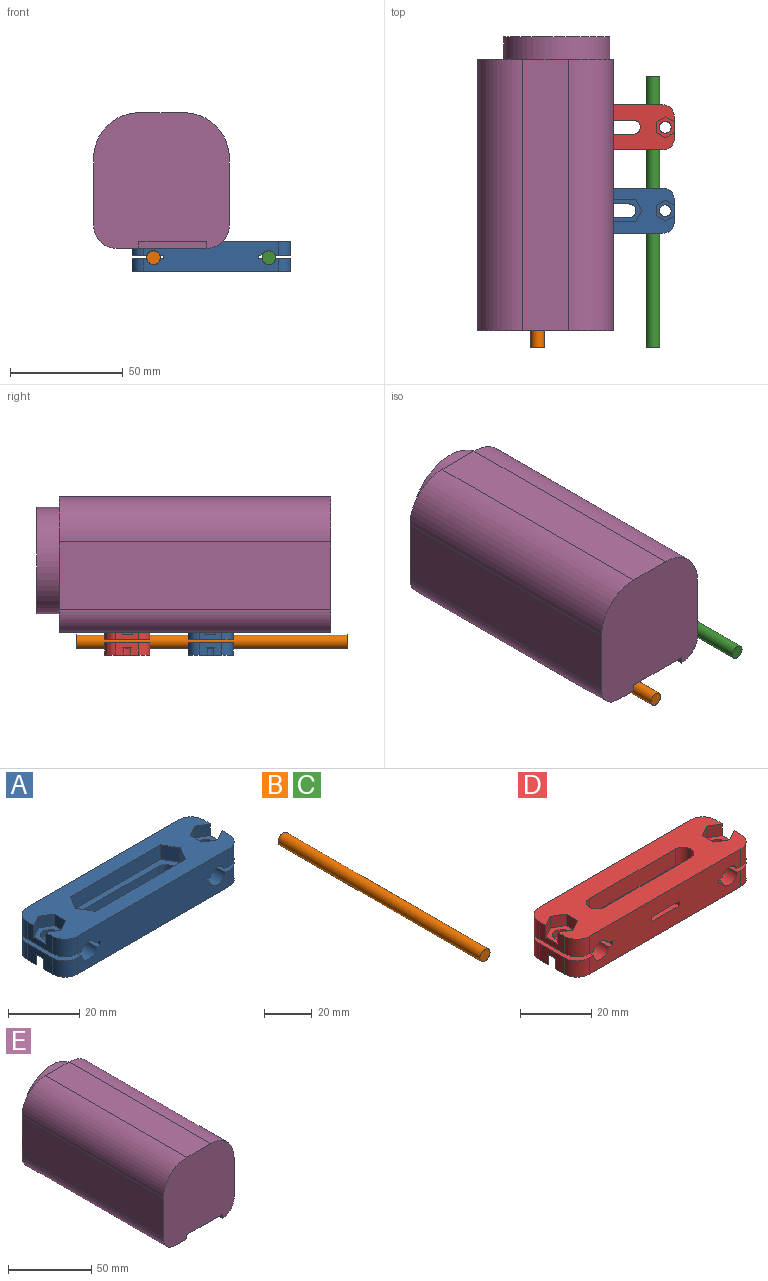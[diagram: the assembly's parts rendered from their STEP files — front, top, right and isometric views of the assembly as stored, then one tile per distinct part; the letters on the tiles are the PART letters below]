
ASSEMBLY  parts=5 mates=5
PART A: 61 faces, bbox 70x20x13 mm
  f0: plane 70x20mm, normal (0,0,1), area 881.1mm2, adj f12,f13,f14,f15,f19,f20,f21,f22
  f1: cylinder r=3mm len=8mm, axis (0,0,1), area 75.4mm2, adj f2,f4,f6,f60
  f2: plane 30x8mm, normal (0,-1,0), area 240mm2, adj f1,f3,f6,f60
  f3: cylinder r=3mm len=8mm, axis (0,0,1), area 75.4mm2, adj f2,f4,f6,f60
  f4: plane 30x8mm, normal (0,1,0), area 240mm2, adj f1,f3,f6,f60
  f5: cylinder r=2.6mm len=5.2mm, axis (0,0,1), area 33.3mm2, adj f34,f48,f51
  f6: plane 70x20mm, normal (0,0,-1), area 1057.7mm2, adj f1,f2,f3,f4,f14,f15,f17,f18
  f7: cylinder r=2.6mm len=5.2mm, axis (0,0,1), area 33.3mm2, adj f37,f46,f53
  f8: plane 20x1.57mm, normal (0,0,-1), area 31.3mm2, adj f14,f15,f32,f49
  f9: plane 20x1.43mm, normal (0,0,1), area 28.5mm2, adj f14,f15,f32,f48
  f10: plane 20x1.57mm, normal (0,0,-1), area 31.3mm2, adj f14,f15,f35,f47
  f11: plane 20x1.43mm, normal (0,0,1), area 28.5mm2, adj f14,f15,f35,f46
  f12: plane 10x6mm, normal (-1,0,0), area 41.5mm2, adj f0,f25,f26,f30,f36,f44,f45
  f13: plane 10x6mm, normal (1,0,0), area 41.5mm2, adj f0,f19,f23,f24,f33,f42,f43
  f14: plane 60x13mm, normal (0,-1,0), area 711.5mm2, adj f0,f6,f8,f9,f10,f11,f32,f33
  f15: plane 60x13mm, normal (0,1,0), area 711.5mm2, adj f0,f6,f8,f9,f10,f11,f32,f33
  f16: cylinder r=2.6mm len=5.2mm, axis (0,0,1), area 32.6mm2, adj f30,f36,f47
  f17: plane 10x5.6mm, normal (-1,0,0), area 45.9mm2, adj f6,f37,f38,f41,f52,f53
  f18: plane 10x5.6mm, normal (1,0,0), area 45.9mm2, adj f6,f34,f39,f40,f50,f51
  f19: plane 4x4mm, normal (-0.5,-0.87,0), area 18.5mm2, adj f0,f13,f20,f24
  f20: plane 4x4mm, normal (0.5,-0.87,0), area 18.5mm2, adj f0,f19,f21,f24
  f21: plane 4.62x4mm, normal (1,0,0), area 18.5mm2, adj f0,f20,f22,f24
  f22: plane 4x4mm, normal (0.5,0.87,0), area 18.5mm2, adj f0,f21,f23,f24
  f23: plane 4x4mm, normal (-0.5,0.87,0), area 18.5mm2, adj f0,f13,f22,f24
  f24: plane 9.24x8mm, normal (0,0,1), area 34.2mm2, adj f13,f19,f20,f21,f22,f23,f31
  f25: plane 4x4mm, normal (0.5,-0.87,0), area 18.5mm2, adj f0,f12,f29,f30
  f26: plane 4x4mm, normal (0.5,0.87,0), area 18.5mm2, adj f0,f12,f27,f30
  f27: plane 4x4mm, normal (-0.5,0.87,0), area 18.5mm2, adj f0,f26,f28,f30
  f28: plane 4.62x4mm, normal (-1,0,0), area 18.5mm2, adj f0,f27,f29,f30
  f29: plane 4x4mm, normal (-0.5,-0.87,0), area 18.5mm2, adj f0,f25,f28,f30
  f30: plane 9.24x8mm, normal (0,0,1), area 34.2mm2, adj f12,f16,f25,f26,f27,f28,f29
  f31: cylinder r=2.6mm len=5.2mm, axis (0,0,1), area 32.6mm2, adj f24,f33,f49
  f32: plane 20x1.4mm, normal (1,0,0), area 28mm2, adj f8,f9,f14,f15
  f33: plane 20x6.57mm, normal (0,0,-1), area 99.4mm2, adj f13,f14,f15,f31,f42,f43,f49
  f34: plane 20x6.43mm, normal (0,0,1), area 96.8mm2, adj f5,f14,f15,f18,f39,f40,f48
  f35: plane 20x1.4mm, normal (-1,0,0), area 28mm2, adj f10,f11,f14,f15
  f36: plane 20x6.57mm, normal (0,0,-1), area 99.4mm2, adj f12,f14,f15,f16,f44,f45,f47
  f37: plane 20x6.43mm, normal (0,0,1), area 96.8mm2, adj f7,f14,f15,f17,f38,f41,f46
  f38: cylinder r=5mm len=5.6mm, axis (0,0,-1), area 44mm2, adj f6,f14,f17,f37
  f39: cylinder r=5mm len=5.6mm, axis (0,0,1), area 44mm2, adj f6,f14,f18,f34
  f40: cylinder r=5mm len=5.6mm, axis (0,0,-1), area 44mm2, adj f6,f15,f18,f34
  f41: cylinder r=5mm len=5.6mm, axis (0,0,1), area 44mm2, adj f6,f15,f17,f37
  f42: cylinder r=5mm len=6mm, axis (0,0,1), area 47.1mm2, adj f0,f13,f14,f33
  f43: cylinder r=5mm len=6mm, axis (0,0,-1), area 47.1mm2, adj f0,f13,f15,f33
  f44: cylinder r=5mm len=6mm, axis (0,0,1), area 47.1mm2, adj f0,f12,f15,f36
  f45: cylinder r=5mm len=6mm, axis (0,0,-1), area 47.1mm2, adj f0,f12,f14,f36
  f46: cylinder r=3.1mm len=20mm, axis (0,-1,0), area 175.8mm2, adj f7,f11,f14,f15,f37,f52,f53
  f47: cylinder r=3.1mm len=20mm, axis (0,-1,0), area 154mm2, adj f10,f14,f15,f16,f36
  f48: cylinder r=3.1mm len=20mm, axis (0,-1,0), area 175.8mm2, adj f5,f9,f14,f15,f34,f50,f51
  f49: cylinder r=3.1mm len=20mm, axis (0,-1,0), area 154mm2, adj f8,f14,f15,f31,f33
  f50: cylinder r=4.25mm len=8.5mm, axis (0,0,-1), area 82.2mm2, adj f6,f18,f48,f51
  f51: plane 8.5x7.67mm, normal (0,0,-1), area 33.3mm2, adj f5,f18,f48,f50
  f52: cylinder r=4.25mm len=8.5mm, axis (0,0,-1), area 82.2mm2, adj f6,f17,f46,f53
  f53: plane 8.5x7.67mm, normal (0,0,-1), area 33.3mm2, adj f7,f17,f46,f52
  f54: plane 5x5mm, normal (-0.87,-0.5,0), area 28.9mm2, adj f0,f55,f59,f60
  f55: plane 35.77x5mm, normal (0,-1,0), area 178.9mm2, adj f0,f54,f56,f60
  f56: plane 5x5mm, normal (0.87,-0.5,0), area 28.9mm2, adj f0,f55,f57,f60
  f57: plane 5x5mm, normal (0.87,0.5,0), area 28.9mm2, adj f0,f56,f58,f60
  f58: plane 35.77x5mm, normal (0,1,0), area 178.9mm2, adj f0,f57,f59,f60
  f59: plane 5x5mm, normal (-0.87,0.5,0), area 28.9mm2, adj f0,f54,f58,f60
  f60: plane 41.55x10mm, normal (0,0,1), area 178.3mm2, adj f1,f2,f3,f4,f54,f55,f56,f57
PART B: 3 faces, bbox 6x120x6 mm
  f0: cylinder r=3mm len=120mm, axis (0,1,0), area 2261.9mm2, adj f1,f2
  f1: plane 6x6mm, normal (0,-1,0), area 28.3mm2, adj f0
  f2: plane 6x6mm, normal (0,1,0), area 28.3mm2, adj f0
PART C: same geometry as B
PART D: 67 faces, bbox 70x20x13 mm
  f0: cylinder r=2.6mm len=5.2mm, axis (0,0,1), area 33.3mm2, adj f13,f59,f66
  f1: plane 70x20mm, normal (0,0,-1), area 1033.7mm2, adj f6,f7,f9,f10,f17,f18,f19,f20
  f2: cylinder r=2.6mm len=5.2mm, axis (0,0,1), area 33.3mm2, adj f21,f61,f64
  f3: plane 10x6mm, normal (-1,0,0), area 41.5mm2, adj f11,f12,f22,f31,f32,f36,f62
  f4: plane 10x6mm, normal (1,0,0), area 41.5mm2, adj f22,f25,f29,f30,f42,f43,f60
  f5: cylinder r=3.1mm len=20mm, axis (0,-1,0), area 154mm2, adj f6,f7,f8,f57,f62
  f6: plane 60x13mm, normal (0,-1,0), area 693.9mm2, adj f1,f5,f9,f12,f13,f15,f21,f22
  f7: plane 60x13mm, normal (0,1,0), area 711.5mm2, adj f1,f5,f10,f11,f13,f21,f22,f43
  f8: cylinder r=2.6mm len=5.2mm, axis (0,0,1), area 32.6mm2, adj f5,f36,f62
  f9: cylinder r=5mm len=5.6mm, axis (0,0,1), area 44mm2, adj f1,f6,f24,f59
  f10: cylinder r=5mm len=5.6mm, axis (0,0,-1), area 44mm2, adj f1,f7,f24,f59
  f11: cylinder r=5mm len=6mm, axis (0,0,1), area 47.1mm2, adj f3,f7,f22,f62
  f12: cylinder r=5mm len=6mm, axis (0,0,-1), area 47.1mm2, adj f3,f6,f22,f62
  f13: cylinder r=3.1mm len=20mm, axis (0,-1,0), area 175.8mm2, adj f0,f6,f7,f55,f59,f65,f66
  f14: plane 11x0.3mm, normal (1,0,0), area 3.3mm2, adj f48,f49,f50,f57
  f15: plane 42x15.5mm, normal (0,0,1), area 279.2mm2, adj f6,f16,f17,f18,f19,f20,f48,f49
  f16: plane 17x1.6mm, normal (0,1,0), area 25.2mm2, adj f15,f47,f50,f51,f53,f54
  f17: cylinder r=3mm len=6mm, axis (0,0,1), area 53.7mm2, adj f1,f15,f18,f20
  f18: plane 34x5.7mm, normal (0,-1,0), area 193.8mm2, adj f1,f15,f17,f19
  f19: cylinder r=3mm len=6mm, axis (0,0,1), area 53.7mm2, adj f1,f15,f18,f20
  f20: plane 34x5.7mm, normal (0,1,0), area 193.8mm2, adj f1,f15,f17,f19
  f21: cylinder r=3.1mm len=20mm, axis (0,-1,0), area 175.8mm2, adj f2,f6,f7,f58,f61,f63,f64
  f22: plane 70x20mm, normal (0,0,1), area 1035.4mm2, adj f3,f4,f6,f7,f11,f12,f25,f26
  f23: plane 10x5.6mm, normal (-1,0,0), area 45.9mm2, adj f1,f44,f45,f61,f63,f64
  f24: plane 10x5.6mm, normal (1,0,0), area 45.9mm2, adj f1,f9,f10,f59,f65,f66
  f25: plane 4x4mm, normal (-0.5,-0.87,0), area 18.5mm2, adj f4,f22,f26,f30
  f26: plane 4x4mm, normal (0.5,-0.87,0), area 18.5mm2, adj f22,f25,f27,f30
  f27: plane 4.62x4mm, normal (1,0,0), area 18.5mm2, adj f22,f26,f28,f30
  f28: plane 4x4mm, normal (0.5,0.87,0), area 18.5mm2, adj f22,f27,f29,f30
  f29: plane 4x4mm, normal (-0.5,0.87,0), area 18.5mm2, adj f4,f22,f28,f30
  f30: plane 9.24x8mm, normal (0,0,1), area 34.2mm2, adj f4,f25,f26,f27,f28,f29,f37
  f31: plane 4x4mm, normal (0.5,-0.87,0), area 18.5mm2, adj f3,f22,f35,f36
  f32: plane 4x4mm, normal (0.5,0.87,0), area 18.5mm2, adj f3,f22,f33,f36
  f33: plane 4x4mm, normal (-0.5,0.87,0), area 18.5mm2, adj f22,f32,f34,f36
  f34: plane 4.62x4mm, normal (-1,0,0), area 18.5mm2, adj f22,f33,f35,f36
  f35: plane 4x4mm, normal (-0.5,-0.87,0), area 18.5mm2, adj f22,f31,f34,f36
  f36: plane 9.24x8mm, normal (0,0,1), area 34.2mm2, adj f3,f8,f31,f32,f33,f34,f35
  f37: cylinder r=2.6mm len=5.2mm, axis (0,0,1), area 32.6mm2, adj f30,f46,f60
  f38: cylinder r=3mm len=6mm, axis (0,0,1), area 53.7mm2, adj f22,f39,f41,f50
  f39: plane 34x5.7mm, normal (0,-1,0), area 193.8mm2, adj f22,f38,f40,f50
  f40: cylinder r=3mm len=6mm, axis (0,0,1), area 53.7mm2, adj f22,f39,f41,f50
  f41: plane 34x5.7mm, normal (0,1,0), area 193.8mm2, adj f22,f38,f40,f50
  f42: cylinder r=5mm len=6mm, axis (0,0,1), area 47.1mm2, adj f4,f6,f22,f60
  f43: cylinder r=5mm len=6mm, axis (0,0,-1), area 47.1mm2, adj f4,f7,f22,f60
  f44: cylinder r=5mm len=5.6mm, axis (0,0,1), area 44mm2, adj f1,f7,f23,f61
  f45: cylinder r=5mm len=5.6mm, axis (0,0,-1), area 44mm2, adj f1,f6,f23,f61
  f46: cylinder r=3.1mm len=20mm, axis (0,-1,0), area 154mm2, adj f6,f7,f37,f54,f60
  f47: plane 11x0.3mm, normal (-1,0,0), area 3.3mm2, adj f16,f49,f50,f54
  f48: plane 17x1.6mm, normal (0,1,0), area 25.3mm2, adj f14,f15,f50,f52,f56,f57
  f49: plane 45x1.6mm, normal (0,-1,0), area 68.1mm2, adj f14,f15,f47,f50,f53,f54,f56,f57
  f50: plane 45x15.5mm, normal (0,0,-1), area 312.2mm2, adj f6,f14,f16,f38,f39,f40,f41,f47
  f51: plane 4.5x1.6mm, normal (-1,0,0), area 7.2mm2, adj f6,f15,f16,f50
  f52: plane 4.5x1.6mm, normal (1,0,0), area 7.2mm2, adj f6,f15,f48,f50
  f53: plane 20x1.4mm, normal (1,0,0), area 13.7mm2, adj f6,f7,f15,f16,f49,f54,f55
  f54: plane 20x1.57mm, normal (0,0,-1), area 14.8mm2, adj f6,f7,f16,f46,f47,f49,f53
  f55: plane 20x1.43mm, normal (0,0,1), area 28.5mm2, adj f6,f7,f13,f53
  f56: plane 20x1.4mm, normal (-1,0,0), area 13.7mm2, adj f6,f7,f15,f48,f49,f57,f58
  f57: plane 20x1.57mm, normal (0,0,-1), area 14.8mm2, adj f5,f6,f7,f14,f48,f49,f56
  f58: plane 20x1.43mm, normal (0,0,1), area 28.5mm2, adj f6,f7,f21,f56
  f59: plane 20x6.43mm, normal (0,0,1), area 96.8mm2, adj f0,f6,f7,f9,f10,f13,f24
  f60: plane 20x6.57mm, normal (0,0,-1), area 99.4mm2, adj f4,f6,f7,f37,f42,f43,f46
  f61: plane 20x6.43mm, normal (0,0,1), area 96.8mm2, adj f2,f6,f7,f21,f23,f44,f45
  f62: plane 20x6.57mm, normal (0,0,-1), area 99.4mm2, adj f3,f5,f6,f7,f8,f11,f12
  f63: cylinder r=4.25mm len=8.5mm, axis (0,0,-1), area 82.2mm2, adj f1,f21,f23,f64
  f64: plane 8.5x7.67mm, normal (0,0,-1), area 33.3mm2, adj f2,f21,f23,f63
  f65: cylinder r=4.25mm len=8.5mm, axis (0,0,-1), area 82.2mm2, adj f1,f13,f24,f66
  f66: plane 8.5x7.67mm, normal (0,0,-1), area 33.3mm2, adj f0,f13,f24,f65
PART E: 18 faces, bbox 60x130x60 mm
  f0: plane 60x60mm, normal (0,-1,0), area 3295.4mm2, adj f1,f3,f4,f5,f8,f9,f10,f11
  f1: plane 120x30mm, normal (1,0,0), area 3600mm2, adj f0,f2,f8,f10
  f2: plane 60x60mm, normal (0,1,0), area 1650.5mm2, adj f1,f3,f4,f5,f8,f9,f10,f11
  f3: plane 120x30mm, normal (-1,0,0), area 3600mm2, adj f0,f2,f9,f11
  f4: plane 120x20mm, normal (0,0,1), area 2400mm2, adj f0,f2,f8,f9
  f5: plane 120x40mm, normal (0,0,-1), area 4021.7mm2, adj f0,f2,f6,f10,f11,f14,f15
  f6: cylinder r=3mm len=7mm, axis (0,0,-1), area 131.9mm2, adj f5,f7
  f7: plane 6x6mm, normal (0,0,-1), area 28.3mm2, adj f6
  f8: cylinder r=20mm len=120mm, axis (0,-1,0), area 3769.9mm2, adj f0,f1,f2,f4
  f9: cylinder r=20mm len=120mm, axis (0,1,0), area 3769.9mm2, adj f0,f2,f3,f4
  f10: cylinder r=10mm len=120mm, axis (0,1,0), area 1885mm2, adj f0,f1,f2,f5,f16
  f11: cylinder r=10mm len=120mm, axis (0,-1,0), area 1885mm2, adj f0,f2,f3,f5
  f12: cylinder r=23.5mm len=47mm, axis (0,-1,0), area 1476.5mm2, adj f2,f13
  f13: plane 47x47mm, normal (0,1,0), area 1734.9mm2, adj f12
  f14: plane 25x3mm, normal (1,0,0), area 75mm2, adj f0,f5,f15,f17
  f15: plane 30x3mm, normal (0,-1,0), area 90mm2, adj f5,f14,f16,f17
  f16: plane 25x3mm, normal (-1,0,0), area 75mm2, adj f0,f10,f15,f17
  f17: plane 30x25mm, normal (0,0,-1), area 750mm2, adj f0,f14,f15,f16
PLACE A t=(7.87,32.44,26.99)mm
PLACE B t=(-17.63,92,26.49)mm fixed
PLACE C t=(33.37,92,26.49)mm fixed
PLACE D t=(7.87,69.34,26.99)mm
PLACE E t=(-14.13,39.34,30.64)mm
MATE slider C.f0 <-> A.f48  axis (0,-1,0) through (33.37,-28,26.49)mm
MATE slider B.f0 <-> D.f5  axis (0,1,0) through (-17.63,92,26.49)mm
MATE slider C.f0 <-> D.f13  axis (0,1,0) through (33.37,92,26.49)mm
MATE pin_slot E.f6 <-> D.f19  axis (0,0,-1) through (-9.13,69.34,30.64)mm
MATE slider A.f46 <-> B.f0  axis (0,-1,0) through (-17.63,22.44,26.49)mm
